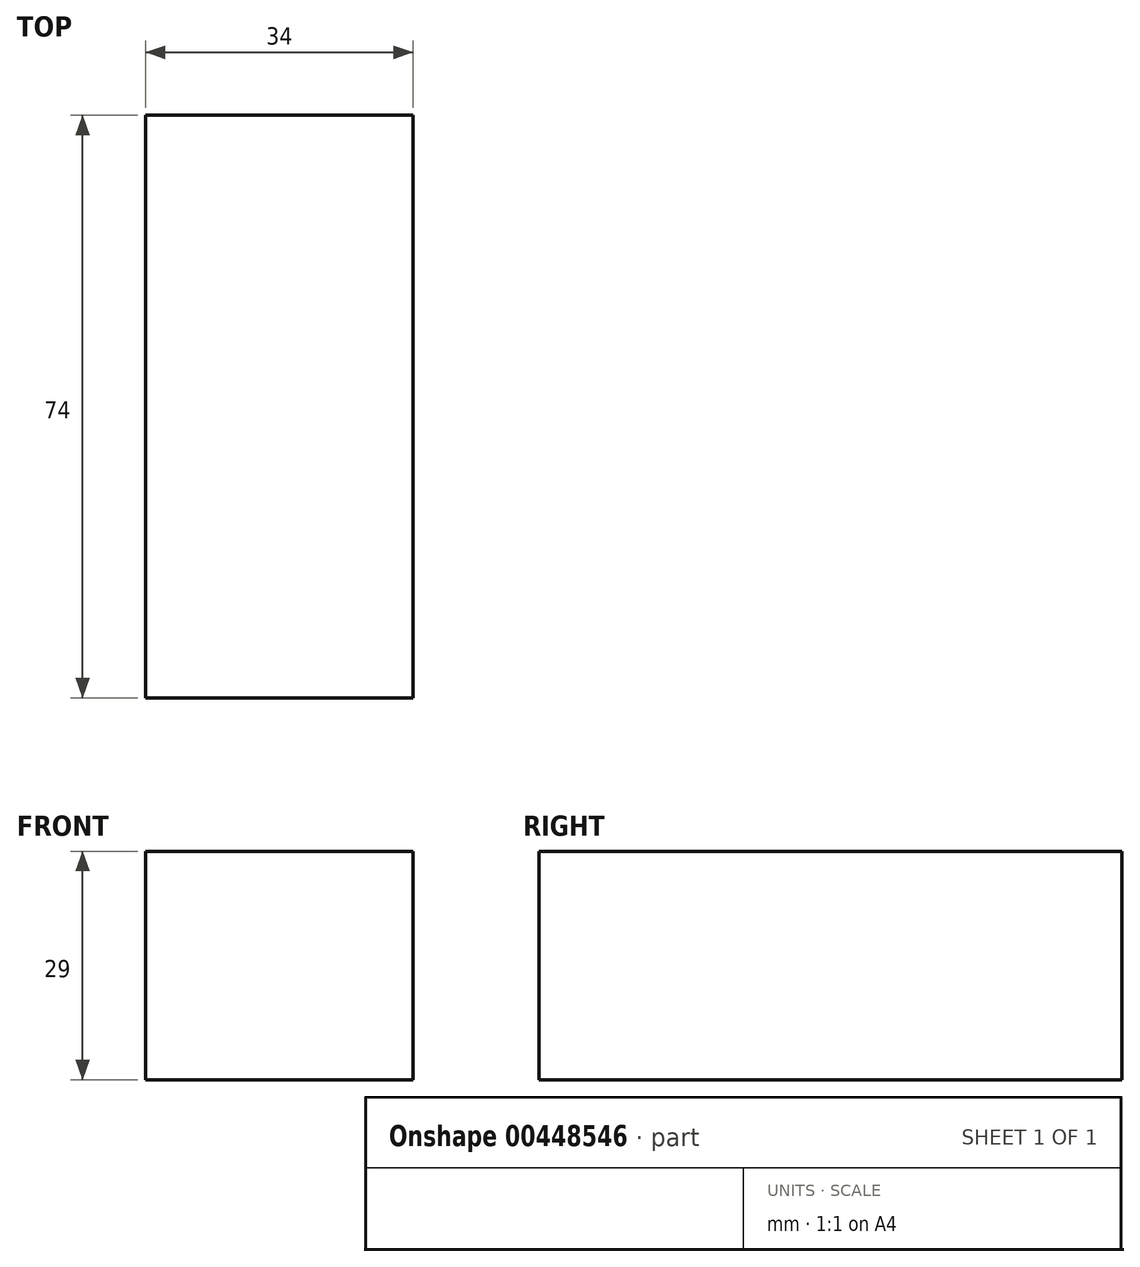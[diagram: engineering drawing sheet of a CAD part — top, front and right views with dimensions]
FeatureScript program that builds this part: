
annotation { "Feature Type Name" : "Feature", "Feature Type Description" : "" }
export const myFeature = defineFeature(function(context is Context, id is Id, definition is map)
    precondition{}
    {
        {
            var Q0;
            Q0=qCreatedBy(makeId("Top.planeOp"),FACE);
            var sketch = newSketch(context, id + "F0", { "sketchPlane" : qUnion([Q0])});
            skLineSegment(sketch, "E0.bottom", {"start": v(17, -37) * mm, "end": v(-17, -37) * mm});
            skLineSegment(sketch, "E0.top", {"start": v(17, 37) * mm, "end": v(-17, 37) * mm});
            skLineSegment(sketch, "E0.left", {"start": v(17, -37) * mm, "end": v(17, 37) * mm});
            skLineSegment(sketch, "E0.right", {"start": v(-17, -37) * mm, "end": v(-17, 37) * mm});
            skPoint(sketch, "E0.middle", {"position": v(0, 0) * mm});
            skSolve(sketch);
        }
        {
            var Q0;
            Q0=makeQuery(id+"F0.imprint","IMPRINT",FACE,{"disambiguationData":[TD([[makeQuery(id+"F0.imprint","IMPRINT",EDGE,{"derivedFrom":sQuery(id+"F0.wireOp",EDGE,"E0.bottom")}),-1.0]])]});
            extrude(context, id + "F1", {"entities" : qUnion([Q0]), "depth" : 29 * mm});
        }
    });
